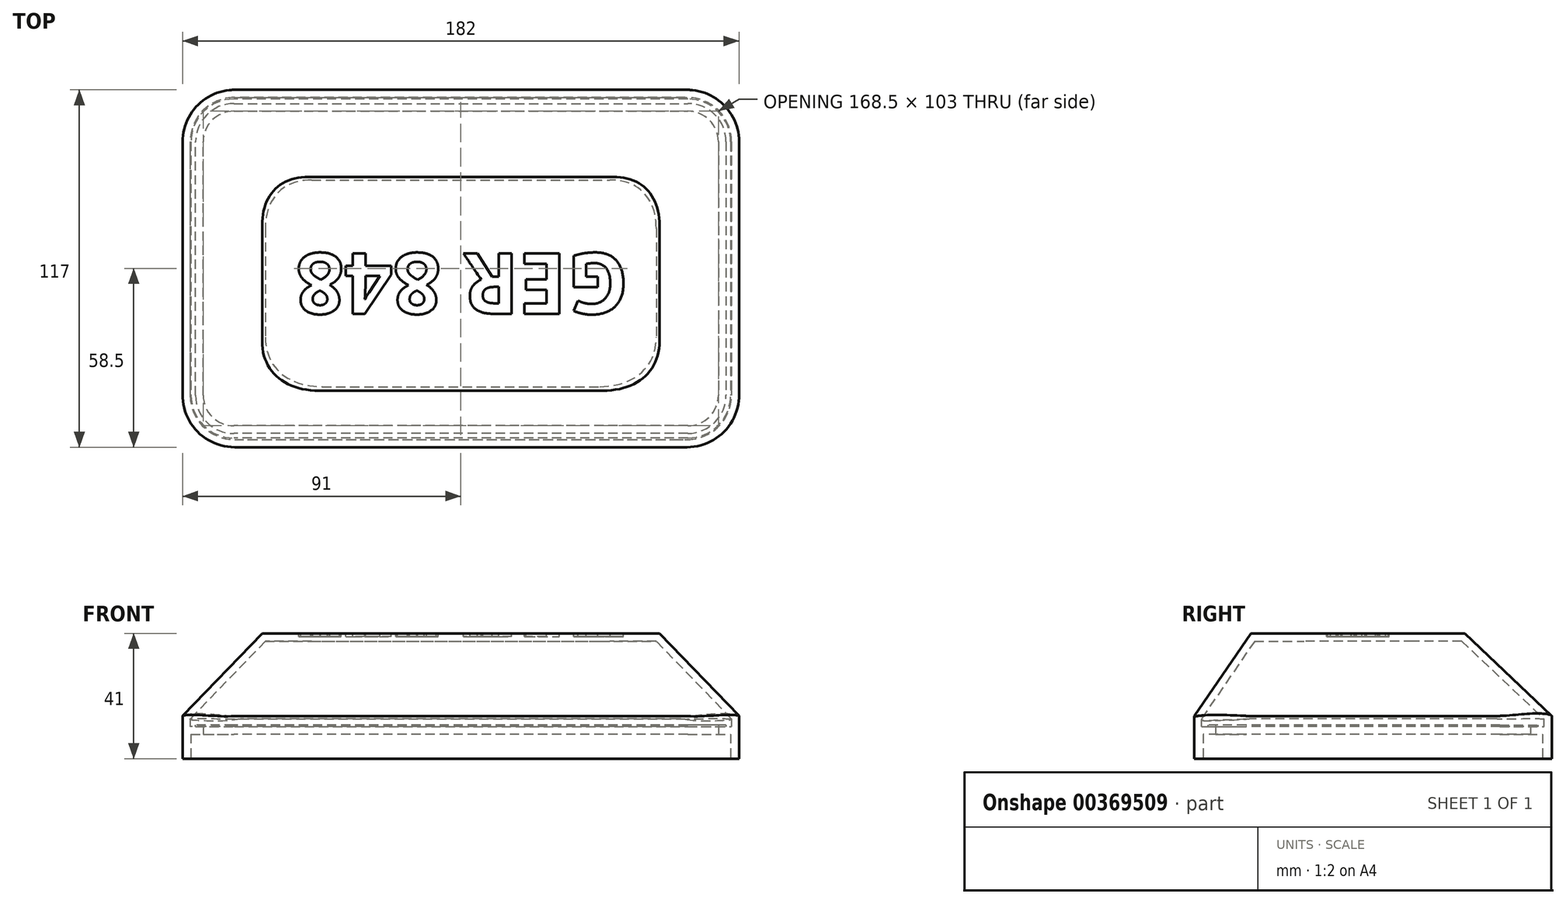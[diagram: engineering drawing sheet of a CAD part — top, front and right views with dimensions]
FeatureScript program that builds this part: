
annotation { "Feature Type Name" : "Feature", "Feature Type Description" : "" }
export const myFeature = defineFeature(function(context is Context, id is Id, definition is map)
    precondition{}
    {
        {
            var Q0;
            Q0=qCreatedBy(makeId("Top.planeOp"),FACE);
            var sketch = newSketch(context, id + "F0", { "sketchPlane" : qUnion([Q0])});
            skLineSegment(sketch, "E0.bottom", {"start": v(-91, 58.5) * mm, "end": v(91, 58.5) * mm});
            skLineSegment(sketch, "E0.top", {"start": v(-91, -58.5) * mm, "end": v(91, -58.5) * mm});
            skLineSegment(sketch, "E0.left", {"start": v(-91, 58.5) * mm, "end": v(-91, -58.5) * mm});
            skLineSegment(sketch, "E0.right", {"start": v(91, 58.5) * mm, "end": v(91, -58.5) * mm});
            skSolve(sketch);
        }
        {
            var Q0;
            Q0=makeQuery(id+"F0.imprint","IMPRINT",FACE,{"disambiguationData":[TD([[makeQuery(id+"F0.imprint","IMPRINT",EDGE,{"derivedFrom":sQuery(id+"F0.wireOp",EDGE,"E0.bottom")}),-1.0]])]});
            extrude(context, id + "F1", {"entities" : qUnion([Q0]), "depth" : 14 * mm});
        }
        {
            var Q0;
            Q0=qCreatedBy(makeId("Top.planeOp"),FACE);
            cPlane(context, id + "F2", {"entities" : qUnion([Q0]), "cplaneType" : CPlaneType.OFFSET, "offset" : 41 * mm, "width" : 150 * mm, "height" : 150 * mm});
        }
        {
            var Q0;
            Q0=qCreatedBy(id+"F2.planeOp",FACE);
            var sketch = newSketch(context, id + "F3", { "sketchPlane" : qUnion([Q0])});
            skLineSegment(sketch, "E1.bottom", {"start": v(-65, 30) * mm, "end": v(65, 30) * mm});
            skLineSegment(sketch, "E1.top", {"start": v(-65, -40) * mm, "end": v(65, -40) * mm});
            skLineSegment(sketch, "E1.left", {"start": v(-65, 30) * mm, "end": v(-65, -40) * mm});
            skLineSegment(sketch, "E1.right", {"start": v(65, 30) * mm, "end": v(65, -40) * mm});
            skSolve(sketch);
        }
        {
            var Q1;
            Q1=makeQuery(id+"F1.opExtrude","CAP_FACE",FACE,{"disambiguationData":[OSD([sQuery(id+"F0.wireOp",EDGE,"E0.bottom"),sQuery(id+"F0.wireOp",EDGE,"E0.top"),sQuery(id+"F0.wireOp",EDGE,"E0.left"),sQuery(id+"F0.wireOp",EDGE,"E0.right")])],"isStart":false});
            var Q2;
            Q2=makeQuery(id+"F3.imprint","IMPRINT",FACE,{"disambiguationData":[TD([[makeQuery(id+"F3.imprint","IMPRINT",EDGE,{"derivedFrom":sQuery(id+"F3.wireOp",EDGE,"E1.bottom")}),-1.0]])]});
            loft(context, id + "F4", {"operationType" : NewBodyOperationType.ADD, "sheetProfilesArray" : [{ "sheetProfileEntities" : qUnion([Q1]) }, { "sheetProfileEntities" : qUnion([Q2]) }]});
        }
        {
            var Q0;
            Q0=makeQuery(id+"F1.opExtrude","SWEPT_EDGE",EDGE,{"disambiguationData":[OSD([sQuery(id+"F0.wireOp",EDGE,"E0.top"),sQuery(id+"F0.wireOp",EDGE,"E0.right")])]});
            var Q1;
            Q1=makeQuery(id+"F1.opExtrude","SWEPT_EDGE",EDGE,{"disambiguationData":[OSD([sQuery(id+"F0.wireOp",EDGE,"E0.bottom"),sQuery(id+"F0.wireOp",EDGE,"E0.right")])]});
            var Q2;
            Q2=makeQuery(id+"F1.opExtrude","SWEPT_EDGE",EDGE,{"disambiguationData":[OSD([sQuery(id+"F0.wireOp",EDGE,"E0.top"),sQuery(id+"F0.wireOp",EDGE,"E0.left")])]});
            var Q3;
            Q3=makeQuery(id+"F1.opExtrude","SWEPT_EDGE",EDGE,{"disambiguationData":[OSD([sQuery(id+"F0.wireOp",EDGE,"E0.bottom"),sQuery(id+"F0.wireOp",EDGE,"E0.left")])]});
            fillet(context, id + "F5", {"entities" : qUnion([Q0, Q1, Q2, Q3]), "radius" : 17 * mm, "tangentPropagation" : true, "allowEdgeOverflow" : false});
        }
        {
            var Q0;
            Q0=qCreatedBy(makeId("Top.planeOp"),FACE);
            var sketch = newSketch(context, id + "F6", { "sketchPlane" : qUnion([Q0])});
            skLineSegment(sketch, "E2.bottom", {"start": v(74.25, 55.5) * mm, "end": v(-74.25, 55.5) * mm});
            skLineSegment(sketch, "E2.top", {"start": v(74.25, -55.5) * mm, "end": v(-74.25, -55.5) * mm});
            skLineSegment(sketch, "E2.left", {"start": v(88.25, 41.5) * mm, "end": v(88.25, -41.5) * mm});
            skLineSegment(sketch, "E2.right", {"start": v(-88.25, 41.5) * mm, "end": v(-88.25, -41.5) * mm});
            skPoint(sketch, "E3.visualSharp", {"position": v(-88.25, 55.5) * mm});
            skArc(sketch, "E3.filletArc", {"start": v(-74.25, 55.5) * mm, "mid": v(-84.15, 51.4) * mm, "end": v(-88.25, 41.5) * mm});
            skPoint(sketch, "E4.visualSharp", {"position": v(-88.25, -55.5) * mm});
            skArc(sketch, "E4.filletArc", {"start": v(-88.25, -41.5) * mm, "mid": v(-84.15, -51.4) * mm, "end": v(-74.25, -55.5) * mm});
            skPoint(sketch, "E5.visualSharp", {"position": v(88.25, -55.5) * mm});
            skArc(sketch, "E5.filletArc", {"start": v(74.25, -55.5) * mm, "mid": v(84.15, -51.4) * mm, "end": v(88.25, -41.5) * mm});
            skPoint(sketch, "E6.visualSharp", {"position": v(88.25, 55.5) * mm});
            skArc(sketch, "E6.filletArc", {"start": v(88.25, 41.5) * mm, "mid": v(84.15, 51.4) * mm, "end": v(74.25, 55.5) * mm});
            skSolve(sketch);
        }
        {
            var Q0;
            Q0 = qSketchRegion(id + "F6", true);
            extrude(context, id + "F7", {"entities" : qUnion([Q0]), "operationType" : NewBodyOperationType.REMOVE, "depth" : 8 * mm});
        }
        {
            var Q0;
            Q0=makeQuery(id+"F7.boolean.opBoolean","COPY",FACE,{"derivedFrom":makeQuery(id+"F7.opExtrude","CAP_FACE",FACE,{"disambiguationData":[OSD([sQuery(id+"F6.wireOp",EDGE,"E2.bottom"),sQuery(id+"F6.wireOp",EDGE,"E2.top"),sQuery(id+"F6.wireOp",EDGE,"E2.left"),sQuery(id+"F6.wireOp",EDGE,"E2.right")])],"isStart":false})});
            var sketch = newSketch(context, id + "F8", { "sketchPlane" : qUnion([Q0])});
            skArc(sketch, "E7.0", {"start": v(84.25, 41.5) * mm, "mid": v(81.32, 48.57) * mm, "end": v(74.25, 51.5) * mm});
            skLineSegment(sketch, "E7.1", {"start": v(84.25, -41.5) * mm, "end": v(84.25, 41.5) * mm});
            skLineSegment(sketch, "E7.2", {"start": v(74.25, 51.5) * mm, "end": v(-74.25, 51.5) * mm});
            skArc(sketch, "E7.3", {"start": v(74.25, -51.5) * mm, "mid": v(81.32, -48.57) * mm, "end": v(84.25, -41.5) * mm});
            skArc(sketch, "E7.4", {"start": v(-74.25, 51.5) * mm, "mid": v(-81.32, 48.57) * mm, "end": v(-84.25, 41.5) * mm});
            skLineSegment(sketch, "E7.5", {"start": v(-84.25, 41.5) * mm, "end": v(-84.25, -41.5) * mm});
            skArc(sketch, "E7.6", {"start": v(-84.25, -41.5) * mm, "mid": v(-81.32, -48.57) * mm, "end": v(-74.25, -51.5) * mm});
            skLineSegment(sketch, "E7.7", {"start": v(-74.25, -51.5) * mm, "end": v(74.25, -51.5) * mm});
            skSolve(sketch);
        }
        {
            var Q0;
            Q0 = qSketchRegion(id + "F8", true);
            extrude(context, id + "F9", {"entities" : qUnion([Q0]), "operationType" : NewBodyOperationType.REMOVE, "oppositeDirection" : true, "depth" : 3 * mm});
        }
        {
            var Q0;
            Q0=makeQuery(id+"F9.boolean.opBoolean","COPY",FACE,{"derivedFrom":makeQuery(id+"F9.opExtrude","CAP_FACE",FACE,{"disambiguationData":[OSD([sQuery(id+"F8.wireOp",EDGE,"E7.0"),sQuery(id+"F8.wireOp",EDGE,"E7.1"),sQuery(id+"F8.wireOp",EDGE,"E7.2"),sQuery(id+"F8.wireOp",EDGE,"E7.3"),sQuery(id+"F8.wireOp",EDGE,"E7.4"),sQuery(id+"F8.wireOp",EDGE,"E7.5"),sQuery(id+"F8.wireOp",EDGE,"E7.6"),sQuery(id+"F8.wireOp",EDGE,"E7.7")])],"isStart":false})});
            shell(context, id + "F10", {"entities" : qUnion([Q0]), "thickness" : 2.5 * mm});
        }
        {
            var Q0;
            Q0=makeQuery(id+"F4.opLoft","SWEPT_EDGE",EDGE,{"disambiguationData":[OSD([sQuery(id+"F0.wireOp",EDGE,"E0.bottom"),sQuery(id+"F0.wireOp",EDGE,"E0.right"),sQuery(id+"F3.wireOp",EDGE,"E1.bottom"),sQuery(id+"F3.wireOp",EDGE,"E1.right")])]});
            var Q1;
            Q1=makeQuery(id+"F4.opLoft","SWEPT_EDGE",EDGE,{"disambiguationData":[OSD([sQuery(id+"F0.wireOp",EDGE,"E0.top"),sQuery(id+"F0.wireOp",EDGE,"E0.right"),sQuery(id+"F3.wireOp",EDGE,"E1.top"),sQuery(id+"F3.wireOp",EDGE,"E1.right")])]});
            var Q2;
            Q2=makeQuery(id+"F4.opLoft","SWEPT_EDGE",EDGE,{"disambiguationData":[OSD([sQuery(id+"F0.wireOp",EDGE,"E0.bottom"),sQuery(id+"F0.wireOp",EDGE,"E0.left"),sQuery(id+"F3.wireOp",EDGE,"E1.bottom"),sQuery(id+"F3.wireOp",EDGE,"E1.left")])]});
            var Q3;
            Q3=makeQuery(id+"F4.opLoft","SWEPT_EDGE",EDGE,{"disambiguationData":[OSD([sQuery(id+"F0.wireOp",EDGE,"E0.top"),sQuery(id+"F0.wireOp",EDGE,"E0.left"),sQuery(id+"F3.wireOp",EDGE,"E1.top"),sQuery(id+"F3.wireOp",EDGE,"E1.left")])]});
            var Q4;
            Q4=makeQuery(id+"F10.opShell","OFFSET_EDGE",EDGE,{"disambiguationData":[OSD([sQuery(id+"F0.wireOp",EDGE,"E0.top"),sQuery(id+"F0.wireOp",EDGE,"E0.left"),sQuery(id+"F3.wireOp",EDGE,"E1.top"),sQuery(id+"F3.wireOp",EDGE,"E1.left")])]});
            var Q5;
            Q5=makeQuery(id+"F10.opShell","OFFSET_EDGE",EDGE,{"disambiguationData":[OSD([sQuery(id+"F0.wireOp",EDGE,"E0.bottom"),sQuery(id+"F0.wireOp",EDGE,"E0.left"),sQuery(id+"F3.wireOp",EDGE,"E1.bottom"),sQuery(id+"F3.wireOp",EDGE,"E1.left")])]});
            var Q6;
            Q6=makeQuery(id+"F10.opShell","OFFSET_EDGE",EDGE,{"disambiguationData":[OSD([sQuery(id+"F0.wireOp",EDGE,"E0.bottom"),sQuery(id+"F0.wireOp",EDGE,"E0.right"),sQuery(id+"F3.wireOp",EDGE,"E1.bottom"),sQuery(id+"F3.wireOp",EDGE,"E1.right")])]});
            var Q7;
            Q7=makeQuery(id+"F10.opShell","OFFSET_EDGE",EDGE,{"disambiguationData":[OSD([sQuery(id+"F0.wireOp",EDGE,"E0.top"),sQuery(id+"F0.wireOp",EDGE,"E0.right"),sQuery(id+"F3.wireOp",EDGE,"E1.top"),sQuery(id+"F3.wireOp",EDGE,"E1.right")])]});
            fillet(context, id + "F11", {"entities" : qUnion([Q0, Q1, Q2, Q3, Q4, Q5, Q6, Q7]), "radius" : 22 * mm, "tangentPropagation" : true, "allowEdgeOverflow" : false});
        }
        {
            var Q0;
            Q0=makeQuery(id+"F4.opLoft","CAP_FACE",FACE,{"disambiguationData":[OSD([makeQuery(id+"F3.imprint","IMPRINT",FACE,{"disambiguationData":[TD([[makeQuery(id+"F3.imprint","IMPRINT",EDGE,{"derivedFrom":sQuery(id+"F3.wireOp",EDGE,"E1.bottom")}),-1.0]])]})])],"isStart":true});
            var sketch = newSketch(context, id + "F12", { "sketchPlane" : qUnion([Q0])});
            skText(sketch, "E8", { "text": "GER 848", "fontName": "OpenSans-Bold.ttf"});
            const initialGuessF12  = {"E8": [0.05481, 0.005, -1, 0, 0.02]};
            skSetInitialGuess(sketch, initialGuessF12);
            skSolve(sketch);
        }
        {
            var Q0;
            Q0 = qSketchRegion(id + "F12", true);
            extrude(context, id + "F13", {"entities" : qUnion([Q0]), "operationType" : NewBodyOperationType.REMOVE, "oppositeDirection" : true, "depth" : 1 * mm});
        }
    });
